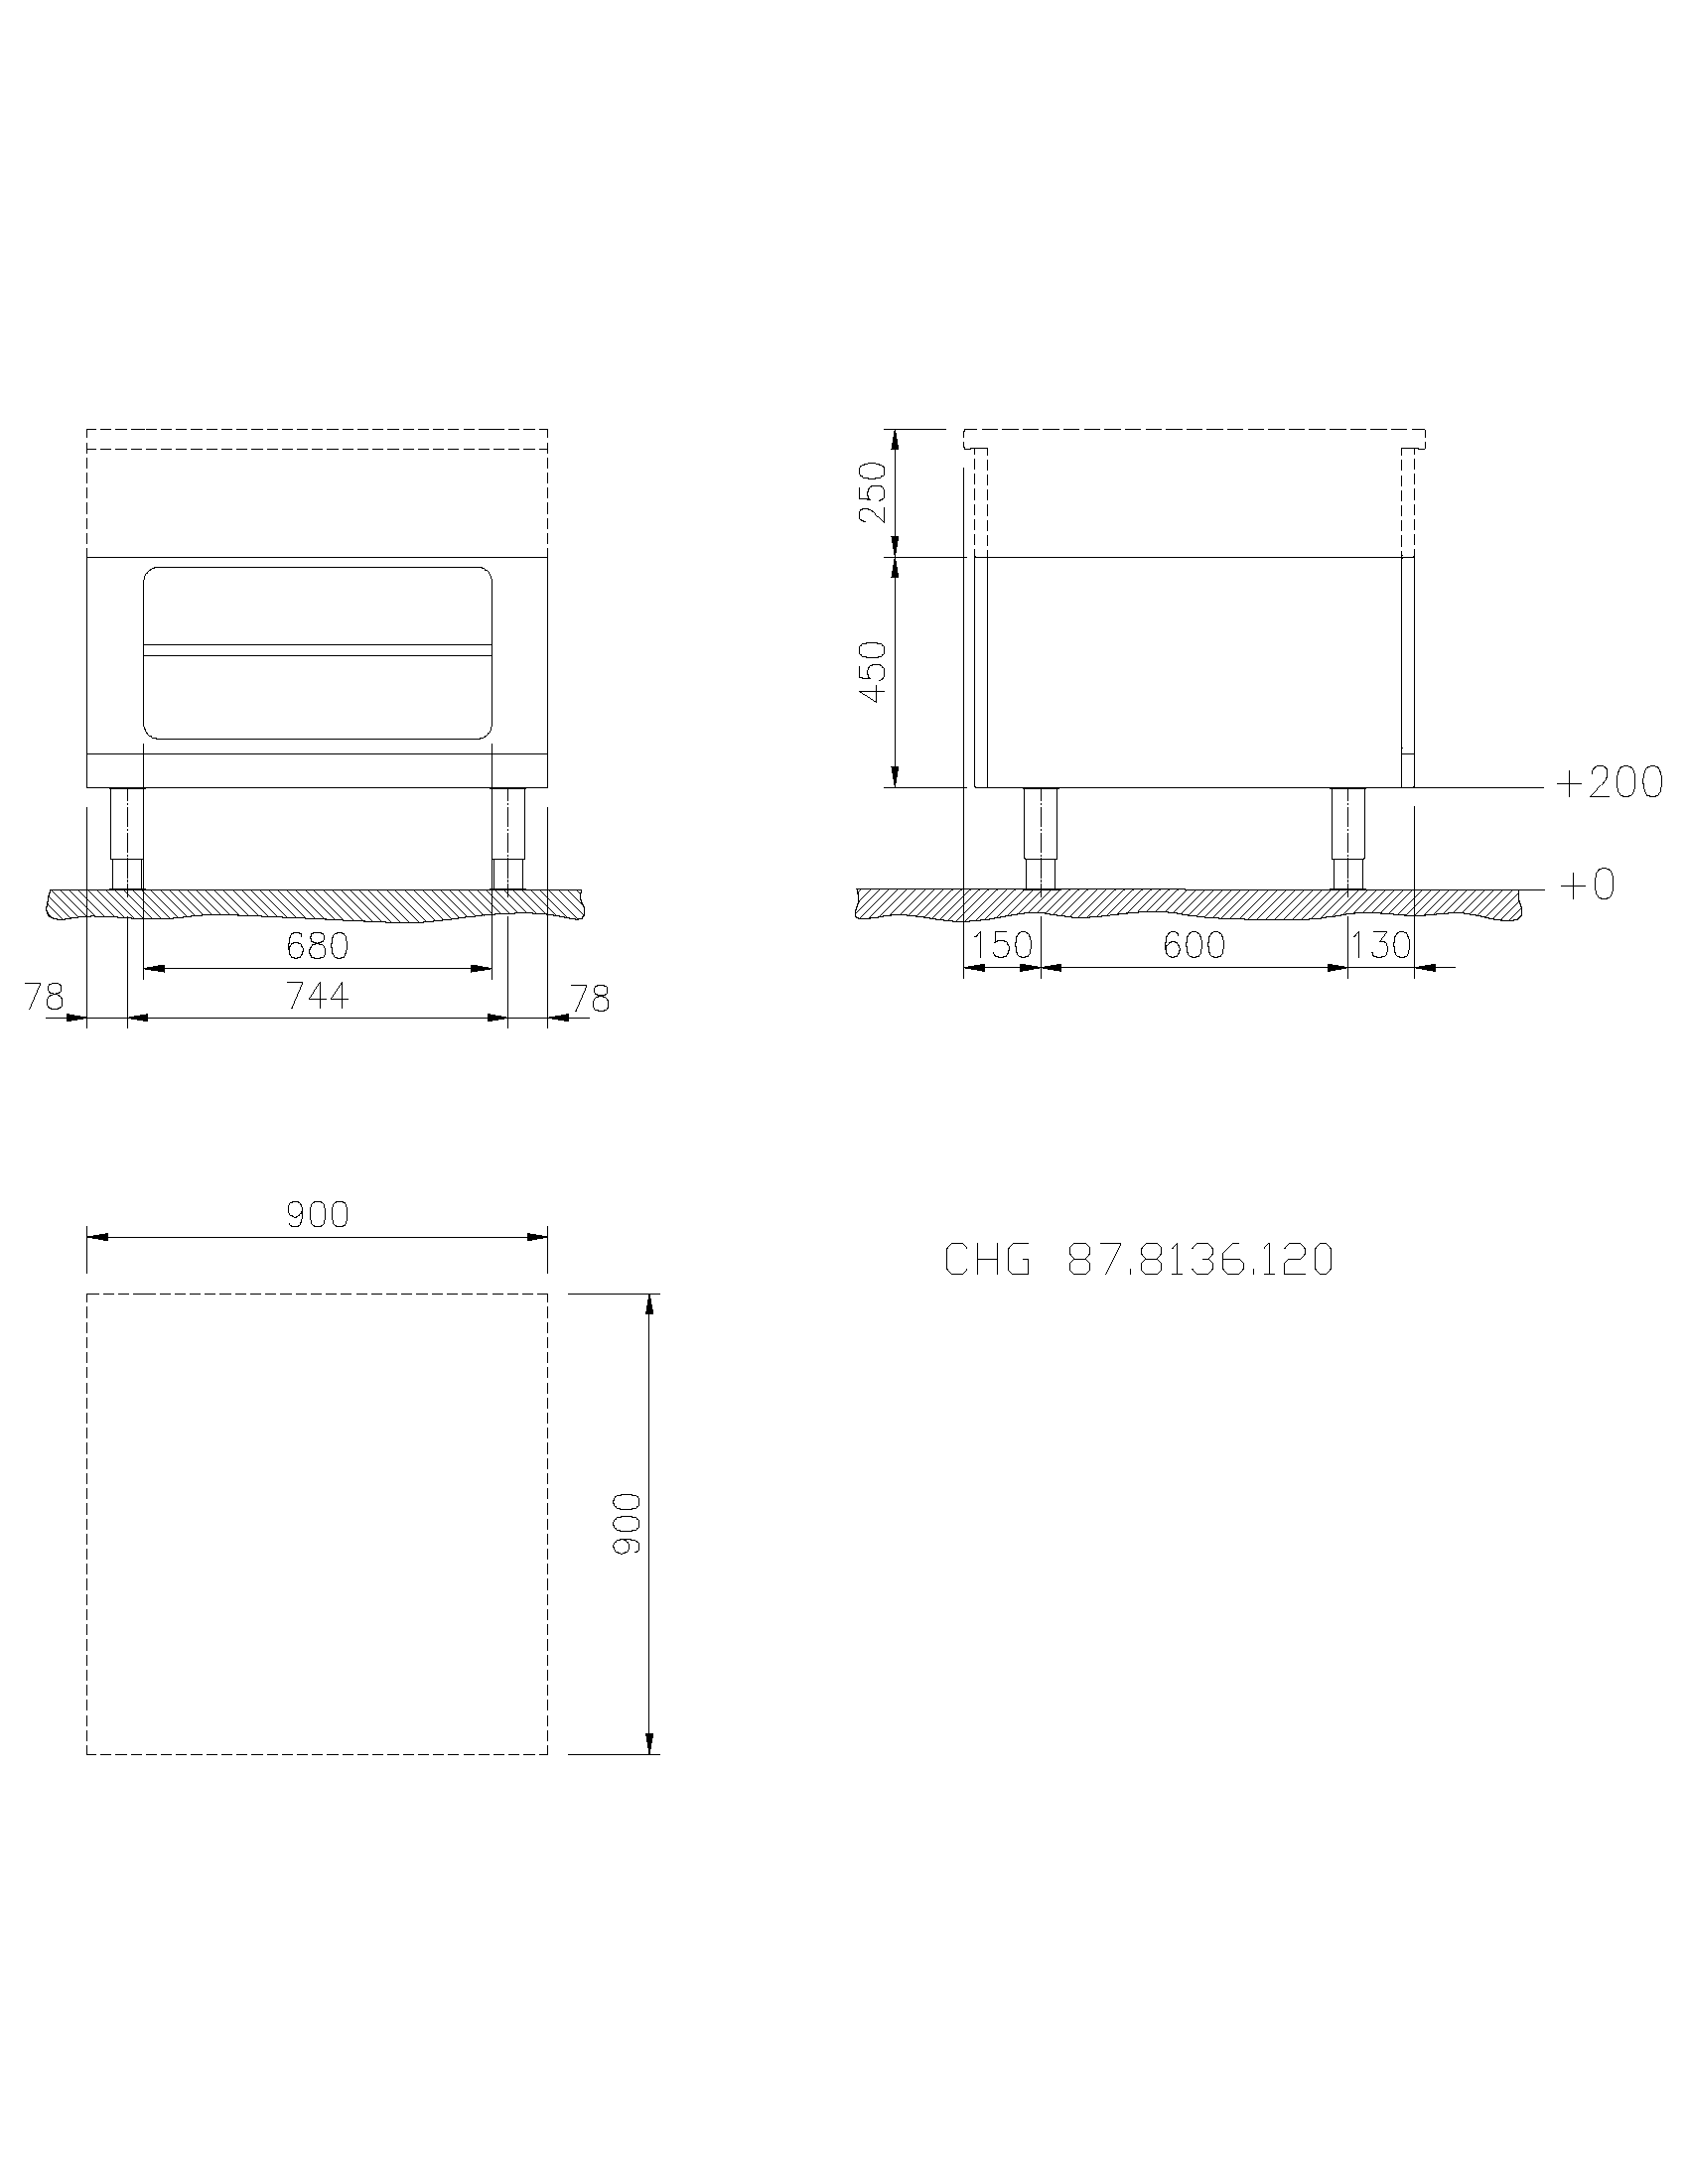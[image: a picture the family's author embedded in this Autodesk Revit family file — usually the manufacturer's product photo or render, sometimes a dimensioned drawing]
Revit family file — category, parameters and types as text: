
# Revit family: QF_ELECTROLUXPROFESSIONAL_589853_MCJQECE1DM
name_source: partatom
category: Attrezzature speciali
units: mm (PartAtom-declared; Revit-internal decimal feet)

## family parameters
Basato su piano di lavoro = No
Condiviso = No
Punto di calcolo locali = No
Quota connettore circolare = Usa diametro
Sempre verticale = Sì
Taglio con vuoti quando caricato = No
Tipo di parte = Normale

## types (1)
- Standard
    Accessory = Sì
    Cold Water Size = 0"
    Compressed Air Pressure = 0.00 psi
    Compressed Air Size = 0"
    Compressed Air Volume = 0 GPM
    Condensate Return Size = 0"
    Cycle = 50 Hz
    Depth Actual = 900 mm  [stored 2.95276 ft]
    Descrizione = FULL IND,OPEN,H3,2Z,2S,500X900X700-MAR
    Direct Waste Size = 0"
    Gas Input Pressure = 0.0
    Gas KW = 0
    Gas Size = 0"
    HP = 18.8 HP
    Height Actual = 700 mm  [stored 2.29659 ft]
    Hot Water Size = 0"
    Item Number = 589853
    Length Actual = 500 mm  [stored 1.64042 ft]
    Modello = MCJQECE1DM
    Phase = 3
    Produttore = Electrolux Professional
    Prospetto di default = 0 mm  [stored 0 ft]
    Refrigerant Compressor Remote = Sì
    Refrigeration Liquid Line Size = 0 mm  [stored 0 ft]
    Refrigeration Suction Line Size = 0 mm  [stored 0 ft]
    Steam Consumption per Hour = 0
    Steam Supply Maximum Pressure = 0.00 psi
    Steam Supply Minimum Pressure = 0.00 psi
    Steam Supply Size = 0"
    URL = https://www.electroluxprofessional.com
    URL Manufacturer = https://www.electroluxprofessional.com
    Volts = 440 V
    Watts = 14000 W
    Weight = 51.00 kg

note: source unit labels omitted for Gas Input Pressure — the stored unit's dimension contradicts the parameter name (converter mislabeling)

note: [stored X ft] marks values corroborated as IEEE doubles in the binary element streams (Revit-internal decimal feet)

## geometry (parser evidence)
native form markers: Blend x13, Sweep x14
no freeform markers — native parametric forms only
